# Revit family: Shower-Shower_Door-KOHLER-Components-K-27619
name_source: partatom
category: Specialty Equipment
revit_build: Autodesk Revit 2017 (Build: 20160225_1515(x64)
units: mm (PartAtom-declared; Revit-internal decimal feet)

## family parameters
Cut with Voids When Loaded = No
Host = Face
OmniClass Number = 23.31.17.17
OmniClass Title = Shower Enclosures
Part Type = Normal
Room Calculation Point = No
Round Connector Dimension = Use Diameter
Shared = No

## types (3) — shared parameters
ADA Compliant = No
Assembly Code = C1030200
Date Modified = 02/08/2021
Default Elevation = 0"
Description = Frameless pivot shower door, 71-3/4inch H x 58 - 58-3/4inch W, with 3/8inch thick Crystal Clear glass
Height = 71 3/4"
Length = 5 7/16"
Manufacturer = KOHLER Co.
Master Format 2014 = 10 28 19.16
Master Format 2014 Name = Shower Doors
Material = Anodized Aluminum
Product Documentation Link = https://www.us.kohler.com
Product Name = Components
Product Page URL = http://www.us.kohler.com
URL = https://www.us.kohler.com
WaterSense Certified = No

## per-type parameters (varying)
| type | Finish | Model | Type |
| SHP-Bright Polished Silver | Kohler-Metal-SHP-Bright_Polished_Silver | K-27619-10L-SHP | 1 |
| BL-Matte Black | Kohler-Metal-BL-Matte_Black | K-27619-10L-BL | 2 |
| BNK-Anodized Brushed Nickel | Kohler-Metal-BNK-Anodized_Brushed_Nickel | K-27619-10L-BNK | 3 |

## geometry (parser evidence)
native form markers: Sweep x6
no freeform markers — native parametric forms only
